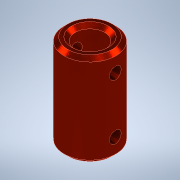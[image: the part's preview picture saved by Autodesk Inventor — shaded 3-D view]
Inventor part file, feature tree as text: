
AUTODESK INVENTOR PART (.ipt)
format: ipt  version: 2021 (Build 250183000, 183)  size: 156,672 bytes
history: native  units: mm
features: extrude x2, sketch x2, chamfer x1
ambient origin geometry x8: Origin, YZ Plane, XZ Plane, XY Plane, X Axis, Y Axis, Z Axis, Center Point
bodies: Solid1 (feature_tree)
feature tree (5):
  extrude  "Extrusion1"  Depth=14.0mm
  chamfer  "Chamfer1"  Distance=25.0mm
  extrude  "Extrusion2"  Depth=5.0mm
  sketch  "Sketch1"  dims[d0=8.0mm d1=14.0mm d2=25.0mm d3=0.0mm]
  sketch  "Sketch2"  dims[d4=1.0mm d5=2.0mm d6=45.0deg d7=3.2mm d8=3.2mm d9=5.0mm d10=5.0mm d11=25.0mm d12=0.0mm]
